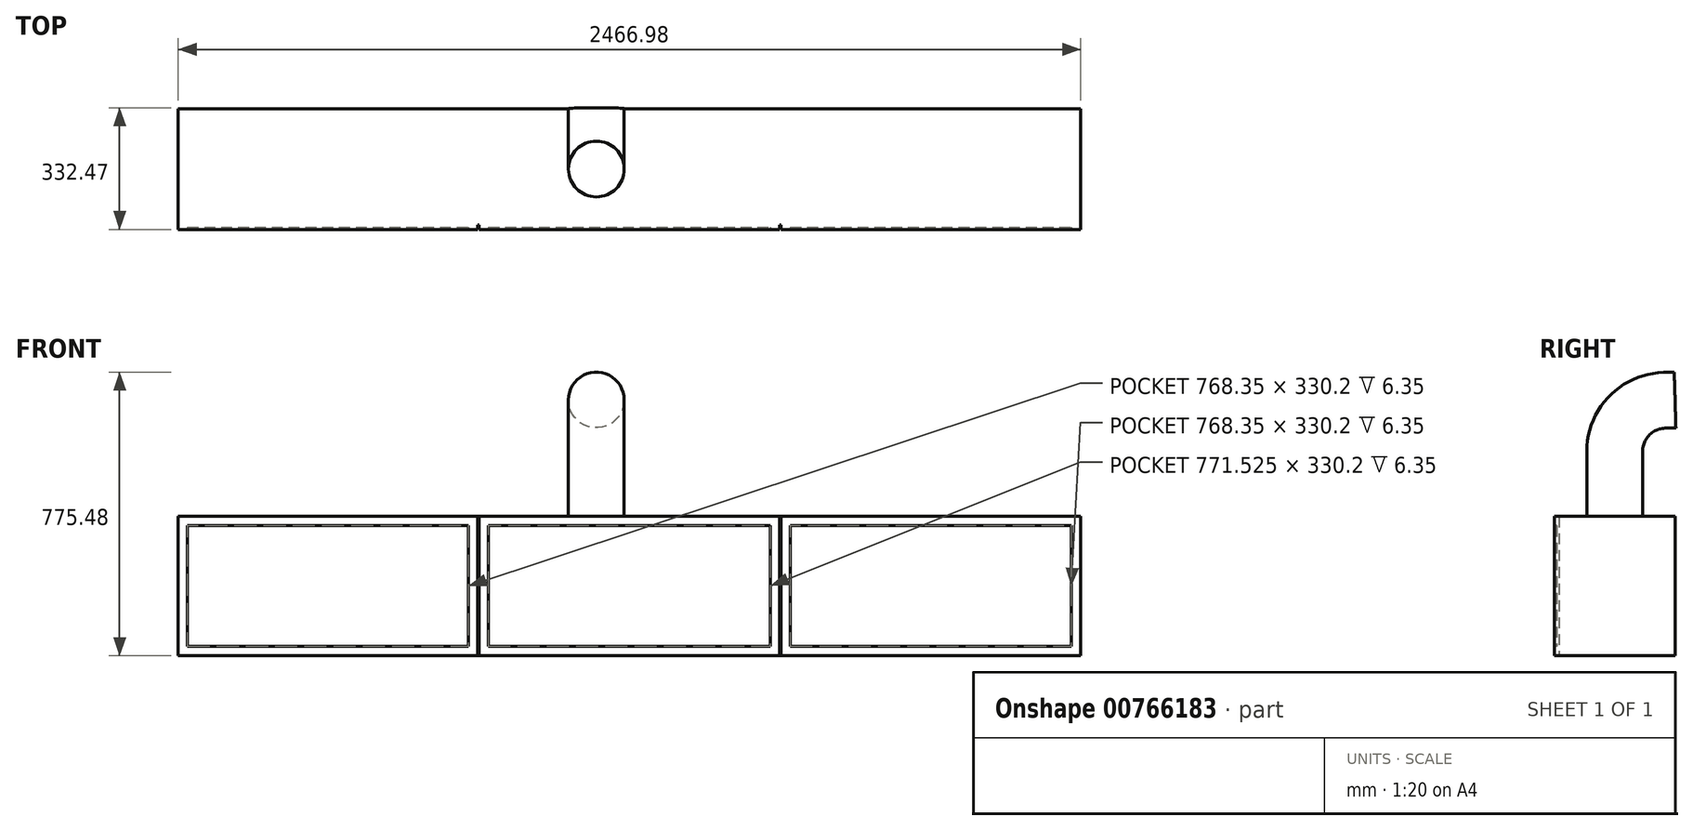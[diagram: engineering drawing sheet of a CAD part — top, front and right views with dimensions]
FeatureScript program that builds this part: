
annotation { "Feature Type Name" : "Feature", "Feature Type Description" : "" }
export const myFeature = defineFeature(function(context is Context, id is Id, definition is map)
    precondition{}
    {
        {
            var Q0;
            Q0=qCreatedBy(makeId("Front.planeOp"),FACE);
            var sketch = newSketch(context, id + "F0", { "sketchPlane" : qUnion([Q0])});
            skLineSegment(sketch, "E0.bottom", {"start": v(1233.49, -190.5) * mm, "end": v(-1233.49, -190.5) * mm});
            skLineSegment(sketch, "E0.top", {"start": v(1233.49, 190.5) * mm, "end": v(-1233.49, 190.5) * mm});
            skLineSegment(sketch, "E0.left", {"start": v(1233.49, -190.5) * mm, "end": v(1233.49, 190.5) * mm});
            skLineSegment(sketch, "E0.right", {"start": v(-1233.49, -190.5) * mm, "end": v(-1233.49, 190.5) * mm});
            skPoint(sketch, "E0.middle", {"position": v(0, 0) * mm});
            skSolve(sketch);
        }
        {
            var Q0;
            Q0=makeQuery(id+"F0.imprint","IMPRINT",FACE,{"disambiguationData":[TD([[makeQuery(id+"F0.imprint","IMPRINT",EDGE,{"derivedFrom":sQuery(id+"F0.wireOp",EDGE,"E0.bottom")}),-1.0]])]});
            extrude(context, id + "F1", {"entities" : qUnion([Q0]), "oppositeDirection" : true, "depth" : 330.2 * mm, "offsetDistance" : 25.4 * mm});
        }
        {
            var Q0;
            Q0=makeQuery(id+"F1.opExtrude","CAP_FACE",FACE,{"disambiguationData":[OSD([sQuery(id+"F0.wireOp",EDGE,"E0.bottom"),sQuery(id+"F0.wireOp",EDGE,"E0.top"),sQuery(id+"F0.wireOp",EDGE,"E0.left"),sQuery(id+"F0.wireOp",EDGE,"E0.right")])],"isStart":true});
            var sketch = newSketch(context, id + "F2", { "sketchPlane" : qUnion([Q0])});
            skLineSegment(sketch, "E1.bottom", {"start": v(-414.34, 190.5) * mm, "end": v(-411.16, 190.5) * mm});
            skLineSegment(sketch, "E1.top", {"start": v(-414.34, -190.5) * mm, "end": v(-411.16, -190.5) * mm});
            skLineSegment(sketch, "E1.left", {"start": v(-414.34, 190.5) * mm, "end": v(-414.34, -190.5) * mm});
            skLineSegment(sketch, "E1.right", {"start": v(-411.16, 190.5) * mm, "end": v(-411.16, -190.5) * mm});
            skLineSegment(sketch, "E2.bottom", {"start": v(411.16, 190.5) * mm, "end": v(414.34, 190.5) * mm});
            skLineSegment(sketch, "E2.top", {"start": v(411.16, -190.5) * mm, "end": v(414.34, -190.5) * mm});
            skLineSegment(sketch, "E2.left", {"start": v(411.16, 190.5) * mm, "end": v(411.16, -190.5) * mm});
            skLineSegment(sketch, "E2.right", {"start": v(414.34, 190.5) * mm, "end": v(414.34, -190.5) * mm});
            skSolve(sketch);
        }
        {
            var Q0;
            Q0=makeQuery(id+"F2.imprint","IMPRINT",FACE,{"disambiguationData":[TD([[makeQuery(id+"F2.imprint","IMPRINT",EDGE,{"derivedFrom":sQuery(id+"F2.wireOp",EDGE,"E1.bottom")}),1.0]])]});
            var Q1;
            Q1=makeQuery(id+"F2.imprint","IMPRINT",FACE,{"disambiguationData":[TD([[makeQuery(id+"F2.imprint","IMPRINT",EDGE,{"derivedFrom":sQuery(id+"F2.wireOp",EDGE,"E2.bottom")}),1.0]])]});
            extrude(context, id + "F3", {"entities" : qUnion([Q0, Q1]), "operationType" : NewBodyOperationType.REMOVE, "oppositeDirection" : true, "depth" : 12.7 * mm, "offsetDistance" : 25.4 * mm});
        }
        {
            var Q0;
            {var subQ0=sQuery(id+"F0.wireOp",EDGE,"E0.bottom");var subQ1=sQuery(id+"F0.wireOp",EDGE,"E0.right");var subQ2=sQuery(id+"F0.wireOp",EDGE,"E0.top");Q0=makeQuery(id+"F3.boolean.opBoolean","SPLIT",FACE,{"disambiguationData":[TD([makeQuery(id+"F1.opExtrude","SWEPT_FACE",FACE,{"disambiguationData":[OSD([subQ1])]})])],"derivedFrom":makeQuery(id+"F1.opExtrude","CAP_FACE",FACE,{"disambiguationData":[OSD([subQ0,subQ2,sQuery(id+"F0.wireOp",EDGE,"E0.left"),subQ1])],"isStart":true})});}
            var sketch = newSketch(context, id + "F4", { "sketchPlane" : qUnion([Q0])});
            skLineSegment(sketch, "E3.bottom", {"start": v(-1208.09, 165.1) * mm, "end": v(-439.74, 165.1) * mm});
            skLineSegment(sketch, "E3.top", {"start": v(-1208.09, -165.1) * mm, "end": v(-439.74, -165.1) * mm});
            skLineSegment(sketch, "E3.left", {"start": v(-1208.09, 165.1) * mm, "end": v(-1208.09, -165.1) * mm});
            skLineSegment(sketch, "E3.right", {"start": v(-439.74, 165.1) * mm, "end": v(-439.74, -165.1) * mm});
            skLineSegment(sketch, "E4.bottom", {"start": v(-385.76, 165.1) * mm, "end": v(385.76, 165.1) * mm});
            skLineSegment(sketch, "E4.top", {"start": v(-385.76, -165.1) * mm, "end": v(385.76, -165.1) * mm});
            skLineSegment(sketch, "E4.left", {"start": v(-385.76, 165.1) * mm, "end": v(-385.76, -165.1) * mm});
            skLineSegment(sketch, "E4.right", {"start": v(385.76, 165.1) * mm, "end": v(385.76, -165.1) * mm});
            skLineSegment(sketch, "E5.bottom", {"start": v(439.74, 165.1) * mm, "end": v(1208.09, 165.1) * mm});
            skLineSegment(sketch, "E5.top", {"start": v(439.74, -165.1) * mm, "end": v(1208.09, -165.1) * mm});
            skLineSegment(sketch, "E5.left", {"start": v(439.74, 165.1) * mm, "end": v(439.74, -165.1) * mm});
            skLineSegment(sketch, "E5.right", {"start": v(1208.09, 165.1) * mm, "end": v(1208.09, -165.1) * mm});
            skSolve(sketch);
        }
        {
            var Q0;
            Q0=makeQuery(id+"F4.imprint","IMPRINT",FACE,{"disambiguationData":[TD([[makeQuery(id+"F4.imprint","IMPRINT",EDGE,{"derivedFrom":sQuery(id+"F4.wireOp",EDGE,"E3.bottom")}),-1.0]])]});
            var Q1;
            Q1=makeQuery(id+"F4.imprint","IMPRINT",FACE,{"disambiguationData":[TD([[makeQuery(id+"F4.imprint","IMPRINT",EDGE,{"derivedFrom":sQuery(id+"F4.wireOp",EDGE,"E4.bottom")}),-1.0]])]});
            var Q2;
            Q2=makeQuery(id+"F4.imprint","IMPRINT",FACE,{"disambiguationData":[TD([[makeQuery(id+"F4.imprint","IMPRINT",EDGE,{"derivedFrom":sQuery(id+"F4.wireOp",EDGE,"E5.bottom")}),-1.0]])]});
            extrude(context, id + "F5", {"entities" : qUnion([Q0, Q1, Q2]), "operationType" : NewBodyOperationType.REMOVE, "oppositeDirection" : true, "depth" : 6.35 * mm, "offsetDistance" : 25.4 * mm});
        }
        {
            var Q0;
            Q0=makeQuery(id+"F1.opExtrude","SWEPT_FACE",FACE,{"disambiguationData":[OSD([sQuery(id+"F0.wireOp",EDGE,"E0.top")])]});
            var sketch = newSketch(context, id + "F6", { "sketchPlane" : qUnion([Q0])});
            skCircle(sketch, "E6", {"center": v(-90.49, 165.1) * mm, "radius": 76.2 * mm});
            skSolve(sketch);
        }
        {
            var Q0;
            Q0=makeQuery(id+"F1.opExtrude","SWEPT_FACE",FACE,{"disambiguationData":[OSD([sQuery(id+"F0.wireOp",EDGE,"E0.right")])]});
            cPlane(context, id + "F7", {"entities" : qUnion([Q0]), "cplaneType" : CPlaneType.OFFSET, "offset" : 1143 * mm, "oppositeDirection" : true, "width" : 152.4 * mm, "height" : 152.4 * mm});
        }
        {
            var Q0;
            Q0=qCreatedBy(id+"F7.planeOp",FACE);
            var sketch = newSketch(context, id + "F8", { "sketchPlane" : qUnion([Q0])});
            skPoint(sketch, "E7.0", {"position": v(-165.1, 190.5) * mm});
            skLineSegment(sketch, "E8", {"start": v(-165.1, 190.5) * mm, "end": v(-165.1, 368.3) * mm});
            skArc(sketch, "E9", {"start": v(-165.1, 368.3) * mm, "mid": v(-204.56, 465.6) * mm, "end": v(-300.64, 507.94) * mm});
            skLineSegment(sketch, "E10.0", {"start": v(-330.2, 190.5) * mm, "end": v(0, 190.5) * mm});
            skLineSegment(sketch, "E11", {"start": v(-300.64, 507.94) * mm, "end": v(-330.2, 508.82) * mm});
            skSolve(sketch);
        }
        {
            var Q0;
            Q0=makeQuery(id+"F6.imprint","IMPRINT",FACE,{"disambiguationData":[TD([[makeQuery(id+"F6.imprint","IMPRINT",EDGE,{"derivedFrom":sQuery(id+"F6.wireOp",EDGE,"E6")}),1.0]])]});
            var Q1;
            Q1=sQuery(id+"F8.wireOp",EDGE,"E9");
            var Q2;
            Q2=sQuery(id+"F8.wireOp",EDGE,"E8");
            var Q3;
            Q3=sQuery(id+"F8.wireOp",EDGE,"E11");
            sweep(context, id + "F9", {"operationType" : NewBodyOperationType.ADD, "profiles" : qUnion([Q0]), "path" : qUnion([Q1, Q2, Q3])});
        }
    });
